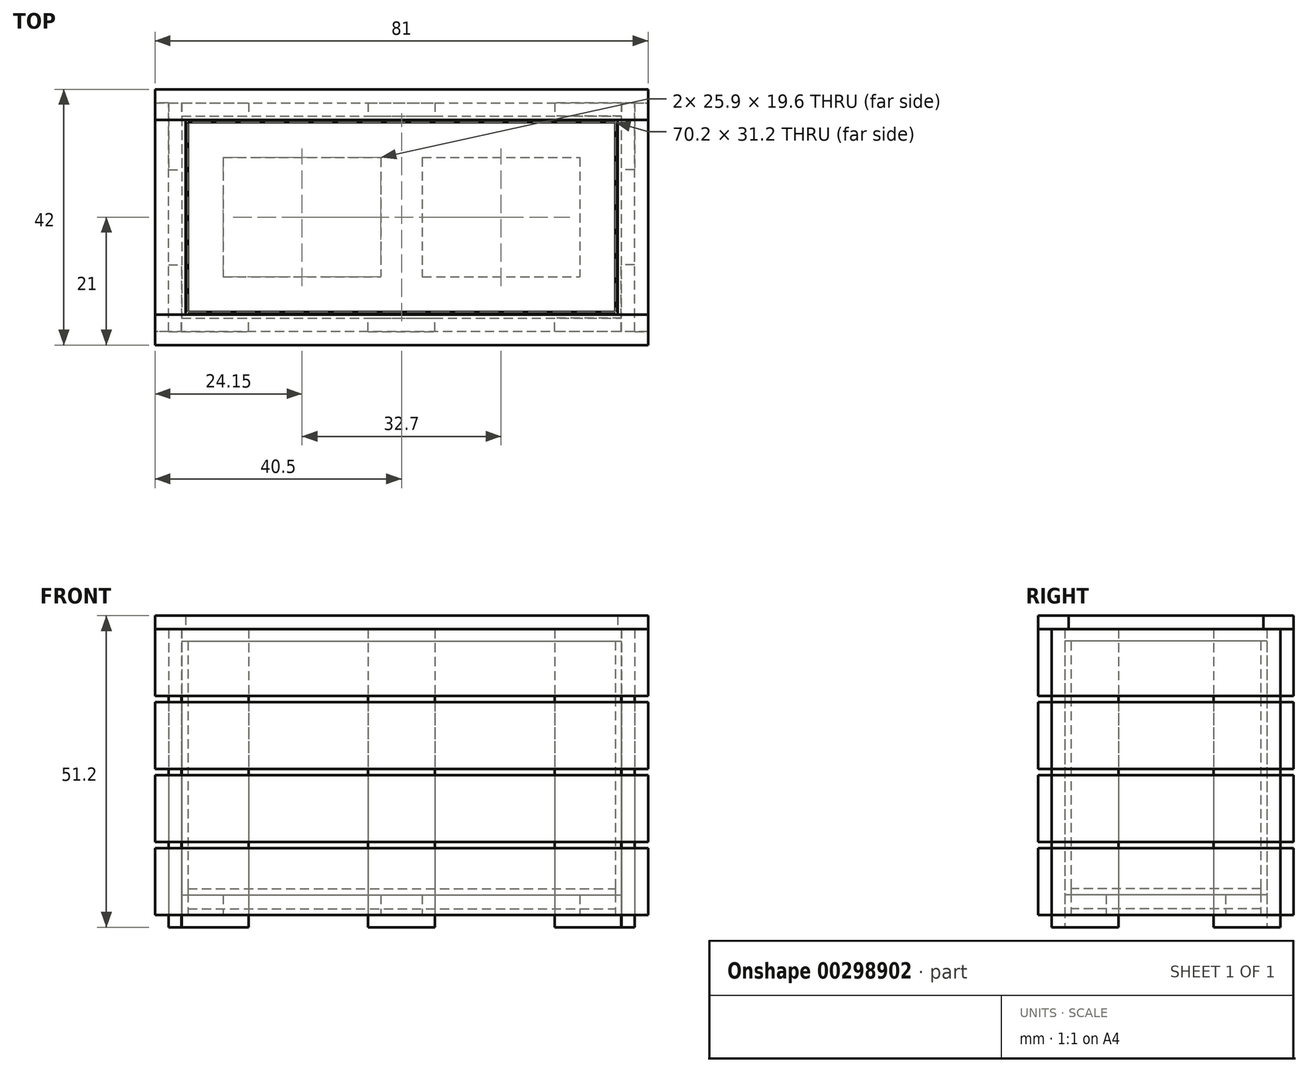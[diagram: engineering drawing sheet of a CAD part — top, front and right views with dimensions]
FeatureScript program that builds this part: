
annotation { "Feature Type Name" : "Feature", "Feature Type Description" : "" }
export const myFeature = defineFeature(function(context is Context, id is Id, definition is map)
    precondition{}
    {
        {
            var Q0;
            Q0=qCreatedBy(makeId("Top.planeOp"),FACE);
            var sketch = newSketch(context, id + "F0", { "sketchPlane" : qUnion([Q0])});
            skLineSegment(sketch, "E0.bottom", {"start": v(-40.5, 21) * mm, "end": v(40.5, 21) * mm});
            skLineSegment(sketch, "E0.top", {"start": v(-40.5, -21) * mm, "end": v(40.5, -21) * mm});
            skLineSegment(sketch, "E0.left", {"start": v(-40.5, 21) * mm, "end": v(-40.5, -21) * mm});
            skLineSegment(sketch, "E0.right", {"start": v(40.5, 21) * mm, "end": v(40.5, -21) * mm});
            skPoint(sketch, "E0.middle", {"position": v(0, 0) * mm});
            skSolve(sketch);
        }
        {
            var Q0;
            Q0=qCreatedBy(makeId("Top.planeOp"),FACE);
            var sketch = newSketch(context, id + "F1", { "sketchPlane" : qUnion([Q0])});
            skLineSegment(sketch, "E1.bottom", {"start": v(-40.5, 21) * mm, "end": v(40.5, 21) * mm});
            skLineSegment(sketch, "E1.top", {"start": v(-40.5, 18.8) * mm, "end": v(40.5, 18.8) * mm});
            skLineSegment(sketch, "E1.left", {"start": v(-40.5, 21) * mm, "end": v(-40.5, 18.8) * mm});
            skLineSegment(sketch, "E1.right", {"start": v(40.5, 21) * mm, "end": v(40.5, 18.8) * mm});
            skLineSegment(sketch, "E2.MirrorCS", {"start": v(-40.5, -21) * mm, "end": v(40.5, -21) * mm});
            skLineSegment(sketch, "E3.MirrorCS", {"start": v(40.5, -21) * mm, "end": v(40.5, -18.8) * mm});
            skLineSegment(sketch, "E4.MirrorCS", {"start": v(-40.5, -18.8) * mm, "end": v(40.5, -18.8) * mm});
            skLineSegment(sketch, "E5.MirrorCS", {"start": v(-40.5, -21) * mm, "end": v(-40.5, -18.8) * mm});
            skSolve(sketch);
        }
        {
            var Q0;
            Q0=qCreatedBy(makeId("Top.planeOp"),FACE);
            var sketch = newSketch(context, id + "F2", { "sketchPlane" : qUnion([Q0])});
            skLineSegment(sketch, "E6.bottom", {"start": v(-40.5, 18.8) * mm, "end": v(-38.3, 18.8) * mm});
            skLineSegment(sketch, "E6.top", {"start": v(-40.5, -18.8) * mm, "end": v(-38.3, -18.8) * mm});
            skLineSegment(sketch, "E6.left", {"start": v(-40.5, 18.8) * mm, "end": v(-40.5, -18.8) * mm});
            skLineSegment(sketch, "E6.right", {"start": v(-38.3, 18.8) * mm, "end": v(-38.3, -18.8) * mm});
            skLineSegment(sketch, "E7.MirrorCS", {"start": v(40.5, 18.8) * mm, "end": v(38.3, 18.8) * mm});
            skLineSegment(sketch, "E8.MirrorCS", {"start": v(38.3, 18.8) * mm, "end": v(38.3, -18.8) * mm});
            skLineSegment(sketch, "E9.MirrorCS", {"start": v(40.5, -18.8) * mm, "end": v(38.3, -18.8) * mm});
            skLineSegment(sketch, "E10.MirrorCS", {"start": v(40.5, 18.8) * mm, "end": v(40.5, -18.8) * mm});
            skSolve(sketch);
        }
        {
            var Q0;
            Q0 = qSketchRegion(id + "F2", true);
            var Q1;
            Q1 = qSketchRegion(id + "F1", true);
            extrude(context, id + "F3", {"entities" : qUnion([Q0, Q1]), "depth" : 47 * mm});
        }
        {
            var Q0;
            Q0=qCreatedBy(makeId("Front.planeOp"),FACE);
            var sketch = newSketch(context, id + "F4", { "sketchPlane" : qUnion([Q0])});
            skLineSegment(sketch, "E11.bottom", {"start": v(-54.96, 12) * mm, "end": v(59.14, 12) * mm});
            skLineSegment(sketch, "E11.top", {"start": v(-54.96, 11) * mm, "end": v(59.14, 11) * mm});
            skLineSegment(sketch, "E11.left", {"start": v(-54.96, 12) * mm, "end": v(-54.96, 11) * mm});
            skLineSegment(sketch, "E11.right", {"start": v(59.14, 12) * mm, "end": v(59.14, 11) * mm});
            skLineSegment(sketch, "E12.bottom", {"start": v(-60.86, 23) * mm, "end": v(60.92, 23) * mm});
            skLineSegment(sketch, "E12.top", {"start": v(-60.86, 24) * mm, "end": v(60.92, 24) * mm});
            skLineSegment(sketch, "E12.left", {"start": v(-60.86, 23) * mm, "end": v(-60.86, 24) * mm});
            skLineSegment(sketch, "E12.right", {"start": v(60.92, 23) * mm, "end": v(60.92, 24) * mm});
            skLineSegment(sketch, "E13.bottom", {"start": v(-61.5, 35) * mm, "end": v(59.46, 35) * mm});
            skLineSegment(sketch, "E13.top", {"start": v(-61.5, 36) * mm, "end": v(59.46, 36) * mm});
            skLineSegment(sketch, "E13.left", {"start": v(-61.5, 35) * mm, "end": v(-61.5, 36) * mm});
            skLineSegment(sketch, "E13.right", {"start": v(59.46, 35) * mm, "end": v(59.46, 36) * mm});
            skSolve(sketch);
        }
        {
            var Q0;
            Q0 = qSketchRegion(id + "F4", true);
            extrude(context, id + "F5", {"entities" : qUnion([Q0]), "operationType" : NewBodyOperationType.REMOVE, "endBound" : BoundingType.SYMMETRIC, "oppositeDirection" : true, "depth" : 60 * mm});
        }
        {
            var Q0;
            Q0=qCreatedBy(makeId("Top.planeOp"),FACE);
            var sketch = newSketch(context, id + "F6", { "sketchPlane" : qUnion([Q0])});
            skLineSegment(sketch, "E14.bottom", {"start": v(-38.3, 18.8) * mm, "end": v(-36.1, 18.8) * mm});
            skLineSegment(sketch, "E14.top", {"start": v(-38.3, 7.8) * mm, "end": v(-36.1, 7.8) * mm});
            skLineSegment(sketch, "E14.left", {"start": v(-38.3, 18.8) * mm, "end": v(-38.3, 7.8) * mm});
            skLineSegment(sketch, "E14.right", {"start": v(-36.1, 18.8) * mm, "end": v(-36.1, 7.8) * mm});
            skLineSegment(sketch, "E15.MirrorCS", {"start": v(-38.3, -18.8) * mm, "end": v(-38.3, -7.8) * mm});
            skLineSegment(sketch, "E16.MirrorCS", {"start": v(-38.3, -7.8) * mm, "end": v(-36.1, -7.8) * mm});
            skLineSegment(sketch, "E17.MirrorCS", {"start": v(-38.3, -18.8) * mm, "end": v(-36.1, -18.8) * mm});
            skLineSegment(sketch, "E18.MirrorCS", {"start": v(-36.1, -18.8) * mm, "end": v(-36.1, -7.8) * mm});
            skLineSegment(sketch, "E19.MirrorCS", {"start": v(38.3, 7.8) * mm, "end": v(36.1, 7.8) * mm});
            skLineSegment(sketch, "E20.MirrorCS", {"start": v(36.1, 18.8) * mm, "end": v(36.1, 7.8) * mm});
            skLineSegment(sketch, "E21.MirrorCS", {"start": v(38.3, 18.8) * mm, "end": v(36.1, 18.8) * mm});
            skLineSegment(sketch, "E22.MirrorCS", {"start": v(38.3, 18.8) * mm, "end": v(38.3, 7.8) * mm});
            skLineSegment(sketch, "E23.MirrorCS", {"start": v(38.3, -7.8) * mm, "end": v(36.1, -7.8) * mm});
            skLineSegment(sketch, "E24.MirrorCS", {"start": v(38.3, -18.8) * mm, "end": v(38.3, -7.8) * mm});
            skLineSegment(sketch, "E25.MirrorCS", {"start": v(38.3, -18.8) * mm, "end": v(36.1, -18.8) * mm});
            skLineSegment(sketch, "E26.MirrorCS", {"start": v(36.1, -18.8) * mm, "end": v(36.1, -7.8) * mm});
            skSolve(sketch);
        }
        {
            var Q0;
            Q0 = qSketchRegion(id + "F6", true);
            extrude(context, id + "F7", {"entities" : qUnion([Q0]), "depth" : 47 * mm, "hasSecondDirection" : true, "secondDirectionOppositeDirection" : true, "secondDirectionDepth" : 2 * mm});
        }
        {
            var Q0;
            Q0=qCreatedBy(makeId("Top.planeOp"),FACE);
            var sketch = newSketch(context, id + "F8", { "sketchPlane" : qUnion([Q0])});
            skLineSegment(sketch, "E27.bottom", {"start": v(-36.16, 18.8) * mm, "end": v(-25.16, 18.8) * mm});
            skLineSegment(sketch, "E27.top", {"start": v(-36.16, 16.6) * mm, "end": v(-25.16, 16.6) * mm});
            skLineSegment(sketch, "E27.left", {"start": v(-36.16, 18.8) * mm, "end": v(-36.16, 16.6) * mm});
            skLineSegment(sketch, "E27.right", {"start": v(-25.16, 18.8) * mm, "end": v(-25.16, 16.6) * mm});
            skLineSegment(sketch, "E28.MirrorCS", {"start": v(-25.16, -18.8) * mm, "end": v(-25.16, -16.6) * mm});
            skLineSegment(sketch, "E29.MirrorCS", {"start": v(-36.16, -16.6) * mm, "end": v(-25.16, -16.6) * mm});
            skLineSegment(sketch, "E30.MirrorCS", {"start": v(-36.16, -18.8) * mm, "end": v(-36.16, -16.6) * mm});
            skLineSegment(sketch, "E31.MirrorCS", {"start": v(-36.16, -18.8) * mm, "end": v(-25.16, -18.8) * mm});
            skLineSegment(sketch, "E32.MirrorCS", {"start": v(25.16, 18.8) * mm, "end": v(25.16, 16.6) * mm});
            skLineSegment(sketch, "E33.MirrorCS", {"start": v(36.16, 16.6) * mm, "end": v(25.16, 16.6) * mm});
            skLineSegment(sketch, "E34.MirrorCS", {"start": v(36.16, 18.8) * mm, "end": v(36.16, 16.6) * mm});
            skLineSegment(sketch, "E35.MirrorCS", {"start": v(36.16, 18.8) * mm, "end": v(25.16, 18.8) * mm});
            skLineSegment(sketch, "E36.MirrorCS", {"start": v(36.16, -16.6) * mm, "end": v(25.16, -16.6) * mm});
            skLineSegment(sketch, "E37.MirrorCS", {"start": v(25.16, -18.8) * mm, "end": v(25.16, -16.6) * mm});
            skLineSegment(sketch, "E38.MirrorCS", {"start": v(36.16, -18.8) * mm, "end": v(25.16, -18.8) * mm});
            skLineSegment(sketch, "E39.MirrorCS", {"start": v(36.16, -18.8) * mm, "end": v(36.16, -16.6) * mm});
            skSolve(sketch);
        }
        {
            var Q0;
            Q0 = qSketchRegion(id + "F8", true);
            extrude(context, id + "F9", {"entities" : qUnion([Q0]), "depth" : 47 * mm, "hasSecondDirection" : true, "secondDirectionOppositeDirection" : true, "secondDirectionDepth" : 2 * mm});
        }
        {
            var Q0;
            Q0=qCreatedBy(makeId("Top.planeOp"),FACE);
            var sketch = newSketch(context, id + "F10", { "sketchPlane" : qUnion([Q0])});
            skLineSegment(sketch, "E40.bottom", {"start": v(-36.1, 16.6) * mm, "end": v(-29.3, 16.6) * mm});
            skLineSegment(sketch, "E40.top", {"start": v(-36.1, -16.6) * mm, "end": v(-29.3, -16.6) * mm});
            skLineSegment(sketch, "E40.left", {"start": v(-36.1, 16.6) * mm, "end": v(-36.1, -16.6) * mm});
            skLineSegment(sketch, "E40.right", {"start": v(-29.3, 16.6) * mm, "end": v(-29.3, -16.6) * mm});
            skLineSegment(sketch, "E41.MirrorCS", {"start": v(36.1, 16.6) * mm, "end": v(29.3, 16.6) * mm});
            skLineSegment(sketch, "E42.MirrorCS", {"start": v(29.3, 16.6) * mm, "end": v(29.3, -16.6) * mm});
            skLineSegment(sketch, "E43.MirrorCS", {"start": v(36.1, -16.6) * mm, "end": v(29.3, -16.6) * mm});
            skLineSegment(sketch, "E44.MirrorCS", {"start": v(36.1, 16.6) * mm, "end": v(36.1, -16.6) * mm});
            skLineSegment(sketch, "E45.bottom", {"start": v(-29.3, 16.6) * mm, "end": v(29.3, 16.6) * mm});
            skLineSegment(sketch, "E45.top", {"start": v(-29.3, 9.8) * mm, "end": v(29.3, 9.8) * mm});
            skLineSegment(sketch, "E45.left", {"start": v(-29.3, 16.6) * mm, "end": v(-29.3, 9.8) * mm});
            skLineSegment(sketch, "E45.right", {"start": v(29.3, 16.6) * mm, "end": v(29.3, 9.8) * mm});
            skLineSegment(sketch, "E46.MirrorCS", {"start": v(-29.3, -9.8) * mm, "end": v(29.3, -9.8) * mm});
            skLineSegment(sketch, "E47.MirrorCS", {"start": v(-29.3, -16.6) * mm, "end": v(-29.3, -9.8) * mm});
            skLineSegment(sketch, "E48.MirrorCS", {"start": v(-29.3, -16.6) * mm, "end": v(29.3, -16.6) * mm});
            skLineSegment(sketch, "E49.MirrorCS", {"start": v(29.3, -16.6) * mm, "end": v(29.3, -9.8) * mm});
            skSolve(sketch);
        }
        {
            var Q0;
            Q0 = qSketchRegion(id + "F10", true);
            extrude(context, id + "F11", {"entities" : qUnion([Q0]), "depth" : 3.3 * mm});
        }
        {
            var Q0;
            Q0=qCreatedBy(makeId("Top.planeOp"),FACE);
            var sketch = newSketch(context, id + "F12", { "sketchPlane" : qUnion([Q0])});
            skLineSegment(sketch, "E50.bottom", {"start": v(-3.4, 9.8) * mm, "end": v(3.4, 9.8) * mm});
            skLineSegment(sketch, "E50.top", {"start": v(-3.4, -9.8) * mm, "end": v(3.4, -9.8) * mm});
            skLineSegment(sketch, "E50.left", {"start": v(-3.4, 9.8) * mm, "end": v(-3.4, -9.8) * mm});
            skLineSegment(sketch, "E50.right", {"start": v(3.4, 9.8) * mm, "end": v(3.4, -9.8) * mm});
            skPoint(sketch, "E50.middle", {"position": v(0, 0) * mm});
            skSolve(sketch);
        }
        {
            var Q0;
            Q0 = qSketchRegion(id + "F12", true);
            extrude(context, id + "F13", {"entities" : qUnion([Q0]), "operationType" : NewBodyOperationType.ADD, "depth" : 3.3 * mm});
        }
        {
            var Q0;
            Q0=qCreatedBy(makeId("Top.planeOp"),FACE);
            var sketch = newSketch(context, id + "F14", { "sketchPlane" : qUnion([Q0])});
            skLineSegment(sketch, "E51.bottom", {"start": v(-36.1, 16.6) * mm, "end": v(36.1, 16.6) * mm});
            skLineSegment(sketch, "E51.top", {"start": v(-36.1, 15.6) * mm, "end": v(36.1, 15.6) * mm});
            skLineSegment(sketch, "E51.left", {"start": v(-36.1, 16.6) * mm, "end": v(-36.1, 15.6) * mm});
            skLineSegment(sketch, "E51.right", {"start": v(36.1, 16.6) * mm, "end": v(36.1, 15.6) * mm});
            skLineSegment(sketch, "E52.MirrorCS", {"start": v(-36.1, -16.6) * mm, "end": v(-36.1, -15.6) * mm});
            skLineSegment(sketch, "E53.MirrorCS", {"start": v(-36.1, -16.6) * mm, "end": v(36.1, -16.6) * mm});
            skLineSegment(sketch, "E54.MirrorCS", {"start": v(36.1, -16.6) * mm, "end": v(36.1, -15.6) * mm});
            skLineSegment(sketch, "E55.MirrorCS", {"start": v(-36.1, -15.6) * mm, "end": v(36.1, -15.6) * mm});
            skLineSegment(sketch, "E56.bottom", {"start": v(-36.1, 15.6) * mm, "end": v(-35.1, 15.6) * mm});
            skLineSegment(sketch, "E56.top", {"start": v(-36.1, -15.6) * mm, "end": v(-35.1, -15.6) * mm});
            skLineSegment(sketch, "E56.left", {"start": v(-36.1, 15.6) * mm, "end": v(-36.1, -15.6) * mm});
            skLineSegment(sketch, "E56.right", {"start": v(-35.1, 15.6) * mm, "end": v(-35.1, -15.6) * mm});
            skLineSegment(sketch, "E57.MirrorCS", {"start": v(36.1, 15.6) * mm, "end": v(35.1, 15.6) * mm});
            skLineSegment(sketch, "E58.MirrorCS", {"start": v(35.1, 15.6) * mm, "end": v(35.1, -15.6) * mm});
            skLineSegment(sketch, "E59.MirrorCS", {"start": v(36.1, -15.6) * mm, "end": v(35.1, -15.6) * mm});
            skLineSegment(sketch, "E60.MirrorCS", {"start": v(36.1, 15.6) * mm, "end": v(36.1, -15.6) * mm});
            skSolve(sketch);
        }
        {
            var Q0;
            Q0 = qSketchRegion(id + "F14", true);
            extrude(context, id + "F15", {"entities" : qUnion([Q0]), "depth" : 45 * mm});
        }
        {
            var Q0;
            Q0=qCreatedBy(makeId("Top.planeOp"),FACE);
            var sketch = newSketch(context, id + "F16", { "sketchPlane" : qUnion([Q0])});
            skLineSegment(sketch, "E61.bottom", {"start": v(-35.1, 15.6) * mm, "end": v(35.1, 15.6) * mm});
            skLineSegment(sketch, "E61.top", {"start": v(-35.1, -15.6) * mm, "end": v(35.1, -15.6) * mm});
            skLineSegment(sketch, "E61.left", {"start": v(-35.1, 15.6) * mm, "end": v(-35.1, -15.6) * mm});
            skLineSegment(sketch, "E61.right", {"start": v(35.1, 15.6) * mm, "end": v(35.1, -15.6) * mm});
            skPoint(sketch, "E61.middle", {"position": v(0, 0) * mm});
            skSolve(sketch);
        }
        {
            var Q0;
            Q0 = qSketchRegion(id + "F16", true);
            extrude(context, id + "F17", {"entities" : qUnion([Q0]), "depth" : 1 * mm});
        }
        {
            var Q0;
            Q0=makeQuery(id+"F3.opExtrude","CAP_FACE",FACE,{"disambiguationData":[OSD([sQuery(id+"F1.wireOp",EDGE,"E1.bottom"),sQuery(id+"F1.wireOp",EDGE,"E1.top"),sQuery(id+"F1.wireOp",EDGE,"E1.left"),sQuery(id+"F1.wireOp",EDGE,"E1.right")])],"isStart":false});
            var sketch = newSketch(context, id + "F18", { "sketchPlane" : qUnion([Q0])});
            skLineSegment(sketch, "E62.bottom", {"start": v(-40.5, 21) * mm, "end": v(40.5, 21) * mm});
            skLineSegment(sketch, "E62.top", {"start": v(-40.5, 16) * mm, "end": v(40.5, 16) * mm});
            skLineSegment(sketch, "E62.left", {"start": v(-40.5, 21) * mm, "end": v(-40.5, 16) * mm});
            skLineSegment(sketch, "E62.right", {"start": v(40.5, 21) * mm, "end": v(40.5, 16) * mm});
            skLineSegment(sketch, "E63.MirrorCS", {"start": v(-40.5, -21) * mm, "end": v(-40.5, -16) * mm});
            skLineSegment(sketch, "E64.MirrorCS", {"start": v(-40.5, -21) * mm, "end": v(40.5, -21) * mm});
            skLineSegment(sketch, "E65.MirrorCS", {"start": v(40.5, -21) * mm, "end": v(40.5, -16) * mm});
            skLineSegment(sketch, "E66.MirrorCS", {"start": v(-40.5, -16) * mm, "end": v(40.5, -16) * mm});
            skSolve(sketch);
        }
        {
            var Q0;
            Q0 = qSketchRegion(id + "F18", true);
            extrude(context, id + "F19", {"entities" : qUnion([Q0]), "depth" : 2.2 * mm});
        }
        {
            var Q0;
            Q0=makeQuery(id+"F3.opExtrude","CAP_FACE",FACE,{"disambiguationData":[OSD([sQuery(id+"F2.wireOp",EDGE,"E6.bottom"),sQuery(id+"F2.wireOp",EDGE,"E6.top"),sQuery(id+"F2.wireOp",EDGE,"E6.left"),sQuery(id+"F2.wireOp",EDGE,"E6.right")])],"isStart":false});
            var sketch = newSketch(context, id + "F20", { "sketchPlane" : qUnion([Q0])});
            skLineSegment(sketch, "E67.bottom", {"start": v(-40.5, 16) * mm, "end": v(-35.5, 16) * mm});
            skLineSegment(sketch, "E67.top", {"start": v(-40.5, -16) * mm, "end": v(-35.5, -16) * mm});
            skLineSegment(sketch, "E67.left", {"start": v(-40.5, 16) * mm, "end": v(-40.5, -16) * mm});
            skLineSegment(sketch, "E67.right", {"start": v(-35.5, 16) * mm, "end": v(-35.5, -16) * mm});
            skLineSegment(sketch, "E68.MirrorCS", {"start": v(40.5, 16) * mm, "end": v(35.5, 16) * mm});
            skLineSegment(sketch, "E69.MirrorCS", {"start": v(35.5, 16) * mm, "end": v(35.5, -16) * mm});
            skLineSegment(sketch, "E70.MirrorCS", {"start": v(40.5, -16) * mm, "end": v(35.5, -16) * mm});
            skLineSegment(sketch, "E71.MirrorCS", {"start": v(40.5, 16) * mm, "end": v(40.5, -16) * mm});
            skSolve(sketch);
        }
        {
            var Q0;
            Q0 = qSketchRegion(id + "F20", true);
            extrude(context, id + "F21", {"entities" : qUnion([Q0]), "depth" : 2.2 * mm});
        }
        {
            var Q0;
            Q0=makeQuery(id+"F13.boolean.opBoolean","MERGE",FACE,{"derivedFrom":[makeQuery(id+"F11.opExtrude","CAP_FACE",FACE,{"disambiguationData":[OSD([sQuery(id+"F10.wireOp",EDGE,"E40.bottom"),sQuery(id+"F10.wireOp",EDGE,"E40.top"),sQuery(id+"F10.wireOp",EDGE,"E40.left"),sQuery(id+"F10.wireOp",EDGE,"E40.right"),sQuery(id+"F10.wireOp",EDGE,"E41.MirrorCS"),sQuery(id+"F10.wireOp",EDGE,"E42.MirrorCS"),sQuery(id+"F10.wireOp",EDGE,"E43.MirrorCS"),sQuery(id+"F10.wireOp",EDGE,"E44.MirrorCS"),sQuery(id+"F10.wireOp",EDGE,"E45.bottom"),sQuery(id+"F10.wireOp",EDGE,"E45.top"),sQuery(id+"F10.wireOp",EDGE,"E46.MirrorCS"),sQuery(id+"F10.wireOp",EDGE,"E48.MirrorCS")])],"isStart":false}),makeQuery(id+"F13.opExtrude","CAP_FACE",FACE,{"disambiguationData":[OSD([sQuery(id+"F12.wireOp",EDGE,"E50.bottom"),sQuery(id+"F12.wireOp",EDGE,"E50.top"),sQuery(id+"F12.wireOp",EDGE,"E50.left"),sQuery(id+"F12.wireOp",EDGE,"E50.right")])],"isStart":false})]});
            var sketch = newSketch(context, id + "F22", { "sketchPlane" : qUnion([Q0])});
            skLineSegment(sketch, "E72.bottom", {"start": v(-35.1, 15.6) * mm, "end": v(35.1, 15.6) * mm});
            skLineSegment(sketch, "E72.top", {"start": v(-35.1, -15.6) * mm, "end": v(35.1, -15.6) * mm});
            skLineSegment(sketch, "E72.left", {"start": v(-35.1, 15.6) * mm, "end": v(-35.1, -15.6) * mm});
            skLineSegment(sketch, "E72.right", {"start": v(35.1, 15.6) * mm, "end": v(35.1, -15.6) * mm});
            skSolve(sketch);
        }
        {
            var Q0;
            Q0 = qSketchRegion(id + "F22", true);
            extrude(context, id + "F23", {"entities" : qUnion([Q0]), "depth" : 1 * mm});
        }
        {
            var Q0;
            Q0=qCreatedBy(makeId("Top.planeOp"),FACE);
            var sketch = newSketch(context, id + "F24", { "sketchPlane" : qUnion([Q0])});
            skLineSegment(sketch, "E73.bottom", {"start": v(-5.5, 18.8) * mm, "end": v(5.5, 18.8) * mm});
            skLineSegment(sketch, "E73.top", {"start": v(-5.5, 16.6) * mm, "end": v(5.5, 16.6) * mm});
            skLineSegment(sketch, "E73.left", {"start": v(-5.5, 18.8) * mm, "end": v(-5.5, 16.6) * mm});
            skLineSegment(sketch, "E73.right", {"start": v(5.5, 18.8) * mm, "end": v(5.5, 16.6) * mm});
            skPoint(sketch, "E73.middle", {"position": v(0, 17.7) * mm});
            skLineSegment(sketch, "E74.MirrorCS", {"start": v(5.5, -18.8) * mm, "end": v(5.5, -16.6) * mm});
            skLineSegment(sketch, "E75.MirrorCS", {"start": v(-5.5, -16.6) * mm, "end": v(5.5, -16.6) * mm});
            skLineSegment(sketch, "E76.MirrorCS", {"start": v(-5.5, -18.8) * mm, "end": v(-5.5, -16.6) * mm});
            skLineSegment(sketch, "E77.MirrorCS", {"start": v(-5.5, -18.8) * mm, "end": v(5.5, -18.8) * mm});
            skSolve(sketch);
        }
        {
            var Q0;
            Q0 = qSketchRegion(id + "F24", true);
            extrude(context, id + "F25", {"entities" : qUnion([Q0]), "depth" : 47 * mm, "hasSecondDirection" : true, "secondDirectionOppositeDirection" : true, "secondDirectionDepth" : 2 * mm});
        }
    });
